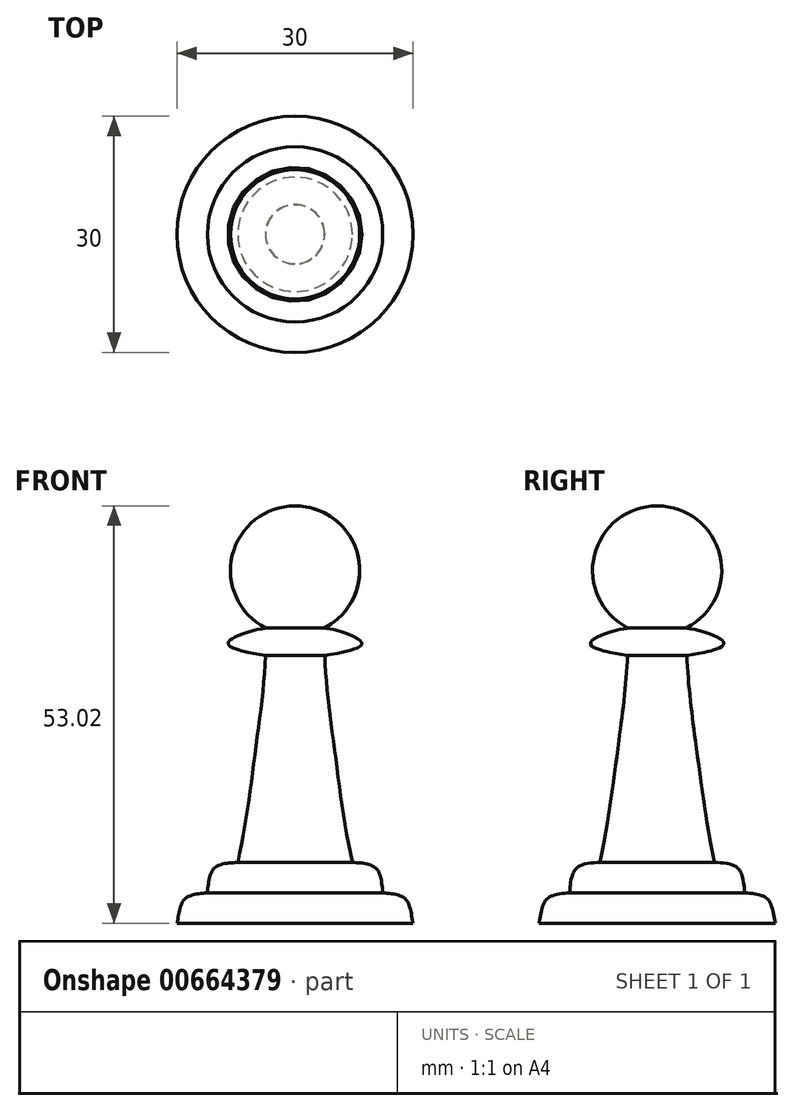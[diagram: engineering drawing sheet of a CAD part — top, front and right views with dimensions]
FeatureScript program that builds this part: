
annotation { "Feature Type Name" : "Feature", "Feature Type Description" : "" }
export const myFeature = defineFeature(function(context is Context, id is Id, definition is map)
    precondition{}
    {
        {
            var Q0;
            Q0=qCreatedBy(makeId("Front.planeOp"),FACE);
            var sketch = newSketch(context, id + "F0", { "sketchPlane" : qUnion([Q0])});
            skArc(sketch, "E0", {"start": v(2.59, 41.75) * mm, "mid": v(6.82, 50.98) * mm, "end": v(-1.16, 57.26) * mm});
            skFitSpline(sketch, "E1", {"points": [v(2.59, 41.75) * mm, v(4.95, 41.22) * mm, v(7.34, 39.77) * mm, v(5.07, 38.7) * mm, v(2.62, 38.28) * mm], "startDerivative": vector(7.23, -1.58) * mm, "endDerivative": vector(-7.42, -0.73) * mm});
            skFitSpline(sketch, "E2", {"points": [v(6.11, 11.97) * mm, v(9.1, 11.24) * mm, v(9.98, 8.1) * mm], "startDerivative": vector(7.13, -0.33) * mm, "endDerivative": vector(0.63, -7.37) * mm});
            skFitSpline(sketch, "E3", {"points": [v(9.98, 8.1) * mm, v(12.83, 7.34) * mm, v(13.84, 4.24) * mm], "startDerivative": vector(6.2, -0.64) * mm, "endDerivative": vector(1.6, -6.98) * mm});
            skLineSegment(sketch, "E4", {"start": v(-1.16, 4.24) * mm, "end": v(13.84, 4.24) * mm});
            skLineSegment(sketch, "E5", {"start": v(-1.16, 57.26) * mm, "end": v(-1.16, 4.24) * mm});
            skFitSpline(sketch, "E6", {"points": [v(2.62, 38.28) * mm, v(3.86, 26.32) * mm, v(6.11, 11.97) * mm], "startDerivative": vector(0.74, -25.06) * mm, "endDerivative": vector(6.17, -27.54) * mm});
            skSolve(sketch);
        }
        {
            var Q0;
            Q0=makeQuery(id+"F0.imprint","IMPRINT",FACE,{"disambiguationData":[TD([[makeQuery(id+"F0.imprint","IMPRINT",EDGE,{"derivedFrom":sQuery(id+"F0.wireOp",EDGE,"E0")}),1.0]])]});
            var Q1;
            Q1=sQuery(id+"F0.wireOp",EDGE,"E5");
            revolve(context, id + "F1", {"entities" : qUnion([Q0]), "axis" : qUnion([Q1]), "revolveType" : RevolveType.FULL});
        }
    });
